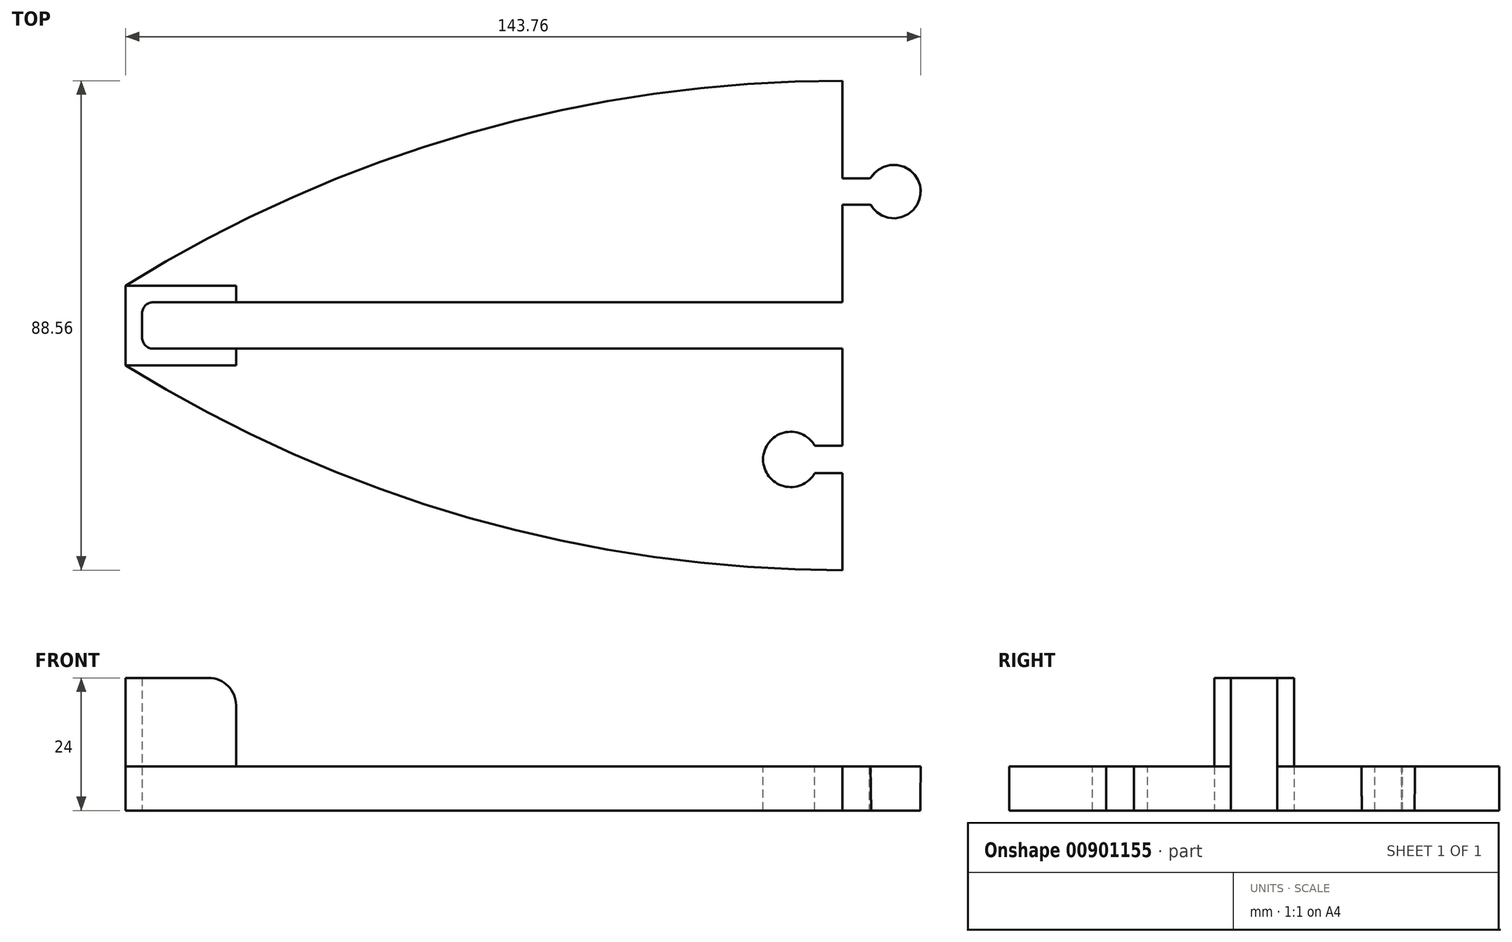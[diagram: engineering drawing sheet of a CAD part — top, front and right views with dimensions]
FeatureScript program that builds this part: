
annotation { "Feature Type Name" : "Feature", "Feature Type Description" : "" }
export const myFeature = defineFeature(function(context is Context, id is Id, definition is map)
    precondition{}
    {
        {
            assignVariable(context, id + "F0", {"name" : "gap", "anyValue" : .1});
        }
        {
            var Q0;
            Q0=qCreatedBy(makeId("Top.planeOp"),FACE);
            var sketch = newSketch(context, id + "F1", { "sketchPlane" : qUnion([Q0])});
            skLineSegment(sketch, "E0.bottom", {"start": v(126.6, -4.2) * mm, "end": v(-126.6, -4.2) * mm});
            skLineSegment(sketch, "E0.top", {"start": v(126.6, 4.2) * mm, "end": v(-126.6, 4.2) * mm});
            skLineSegment(sketch, "E0.left", {"start": v(126.6, -4.2) * mm, "end": v(126.6, 4.2) * mm});
            skLineSegment(sketch, "E0.right", {"start": v(-126.6, -4.2) * mm, "end": v(-126.6, 4.2) * mm});
            skPoint(sketch, "E0.middle", {"position": v(0, 0) * mm});
            skLineSegment(sketch, "E1.bottom", {"start": v(129.6, -7.2) * mm, "end": v(-129.6, -7.2) * mm});
            skLineSegment(sketch, "E1.top", {"start": v(129.6, 7.2) * mm, "end": v(-129.6, 7.2) * mm});
            skLineSegment(sketch, "E1.left", {"start": v(129.6, -7.2) * mm, "end": v(129.6, 7.2) * mm});
            skLineSegment(sketch, "E1.right", {"start": v(-129.6, -7.2) * mm, "end": v(-129.6, 7.2) * mm});
            skSolve(sketch);
        }
        {
            var Q0;
            Q0=qSketchRegion(id+"F1",true);
            extrude(context, id + "F2", {"entities" : qUnion([Q0]), "depth" : 24 * mm, "offsetDistance" : 25 * mm});
        }
        {
            var Q0;
            Q0=makeQuery(id+"F2.opExtrude","SWEPT_EDGE",EDGE,{"disambiguationData":[OSD([sQuery(id+"F1.wireOp",EDGE,"E0.bottom"),sQuery(id+"F1.wireOp",EDGE,"E0.left")])]});
            var Q1;
            Q1=makeQuery(id+"F2.opExtrude","SWEPT_EDGE",EDGE,{"disambiguationData":[OSD([sQuery(id+"F1.wireOp",EDGE,"E0.top"),sQuery(id+"F1.wireOp",EDGE,"E0.left")])]});
            var Q2;
            Q2=makeQuery(id+"F2.opExtrude","SWEPT_EDGE",EDGE,{"disambiguationData":[OSD([sQuery(id+"F1.wireOp",EDGE,"E0.bottom"),sQuery(id+"F1.wireOp",EDGE,"E0.right")])]});
            var Q3;
            Q3=makeQuery(id+"F2.opExtrude","SWEPT_EDGE",EDGE,{"disambiguationData":[OSD([sQuery(id+"F1.wireOp",EDGE,"E0.top"),sQuery(id+"F1.wireOp",EDGE,"E0.right")])]});
            fillet(context, id + "F3", {"entities" : qUnion([Q0, Q1, Q2, Q3]), "radius" : 2 * mm, "tangentPropagation" : true, "allowEdgeOverflow" : false});
        }
        {
            var Q0;
            Q0=qCreatedBy(makeId("Front.planeOp"),FACE);
            var sketch = newSketch(context, id + "F4", { "sketchPlane" : qUnion([Q0])});
            skArc(sketch, "E2", {"start": v(118.6, 0.75) * mm, "mid": v(124.26, 3.1) * mm, "end": v(126.6, 8.75) * mm});
            skLineSegment(sketch, "E3", {"start": v(126.6, 8.75) * mm, "end": v(129.6, 8.75) * mm});
            skLineSegment(sketch, "E4", {"start": v(129.6, 8.75) * mm, "end": v(129.6, 0) * mm});
            skLineSegment(sketch, "E5", {"start": v(118.6, 0.75) * mm, "end": v(118.6, 0) * mm});
            skLineSegment(sketch, "E6", {"start": v(118.6, 0) * mm, "end": v(129.6, 0) * mm});
            skSolve(sketch);
        }
        {
            var Q0;
            Q0=qSketchRegion(id+"F4",true);
            extrude(context, id + "F5", {"entities" : qUnion([Q0]), "operationType" : NewBodyOperationType.ADD, "endBound" : BoundingType.SYMMETRIC, "depth" : (8.5 + (2 * getVariable(context, 'gap'))) * mm, "offsetDistance" : 25 * mm});
        }
        {
            var Q0;
            Q0=makeQuery(id+"F2.opExtrude","CAP_FACE",FACE,{"disambiguationData":[OSD([sQuery(id+"F1.wireOp",EDGE,"E0.bottom"),sQuery(id+"F1.wireOp",EDGE,"E0.top"),sQuery(id+"F1.wireOp",EDGE,"E0.left"),sQuery(id+"F1.wireOp",EDGE,"E0.right"),sQuery(id+"F1.wireOp",EDGE,"E1.bottom"),sQuery(id+"F1.wireOp",EDGE,"E1.top"),sQuery(id+"F1.wireOp",EDGE,"E1.left"),sQuery(id+"F1.wireOp",EDGE,"E1.right")])],"isStart":false});
            var sketch = newSketch(context, id + "F6", { "sketchPlane" : qUnion([Q0])});
            skLineSegment(sketch, "E7.bottom", {"start": v(-109.6, -7.2) * mm, "end": v(109.6, -7.2) * mm});
            skLineSegment(sketch, "E7.top", {"start": v(-109.6, 7.2) * mm, "end": v(109.6, 7.2) * mm});
            skLineSegment(sketch, "E7.left", {"start": v(-109.6, -7.2) * mm, "end": v(-109.6, 7.2) * mm});
            skLineSegment(sketch, "E7.right", {"start": v(109.6, -7.2) * mm, "end": v(109.6, 7.2) * mm});
            skSolve(sketch);
        }
        {
            var Q0;
            Q0=qSketchRegion(id+"F6",true);
            extrude(context, id + "F7", {"entities" : qUnion([Q0]), "operationType" : NewBodyOperationType.REMOVE, "oppositeDirection" : true, "depth" : 16 * mm, "offsetDistance" : 25 * mm});
        }
        {
            var Q0;
            {var subQ1=sQuery(id+"F1.wireOp",EDGE,"E0.top");var subQ2=sQuery(id+"F6.wireOp",EDGE,"E7.left");Q0=makeQuery(id+"F7.boolean.opBoolean","COPY",EDGE,{"disambiguationData":[TD([makeQuery(id+"F2.opExtrude","SWEPT_FACE",FACE,{"disambiguationData":[OSD([subQ1])]})])],"derivedFrom":makeQuery(id+"F7.opExtrude","CAP_EDGE",EDGE,{"disambiguationData":[OSD([subQ2])],"isStart":true})});}
            var Q1;
            {var subQ0=sQuery(id+"F1.wireOp",EDGE,"E0.bottom");var subQ1=sQuery(id+"F6.wireOp",EDGE,"E7.left");Q1=makeQuery(id+"F7.boolean.opBoolean","COPY",EDGE,{"disambiguationData":[TD([makeQuery(id+"F2.opExtrude","SWEPT_FACE",FACE,{"disambiguationData":[OSD([subQ0])]})])],"derivedFrom":makeQuery(id+"F7.opExtrude","CAP_EDGE",EDGE,{"disambiguationData":[OSD([subQ1])],"isStart":true})});}
            var Q2;
            {var subQ1=sQuery(id+"F1.wireOp",EDGE,"E0.top");var subQ2=sQuery(id+"F6.wireOp",EDGE,"E7.right");Q2=makeQuery(id+"F7.boolean.opBoolean","COPY",EDGE,{"disambiguationData":[TD([makeQuery(id+"F2.opExtrude","SWEPT_FACE",FACE,{"disambiguationData":[OSD([subQ1])]})])],"derivedFrom":makeQuery(id+"F7.opExtrude","CAP_EDGE",EDGE,{"disambiguationData":[OSD([subQ2])],"isStart":true})});}
            var Q3;
            {var subQ0=sQuery(id+"F1.wireOp",EDGE,"E0.bottom");var subQ2=sQuery(id+"F6.wireOp",EDGE,"E7.right");Q3=makeQuery(id+"F7.boolean.opBoolean","COPY",EDGE,{"disambiguationData":[TD([makeQuery(id+"F2.opExtrude","SWEPT_FACE",FACE,{"disambiguationData":[OSD([subQ0])]})])],"derivedFrom":makeQuery(id+"F7.opExtrude","CAP_EDGE",EDGE,{"disambiguationData":[OSD([subQ2])],"isStart":true})});}
            fillet(context, id + "F8", {"entities" : qUnion([Q0, Q1, Q2, Q3]), "radius" : 5 * mm, "tangentPropagation" : true, "allowEdgeOverflow" : false});
        }
        {
            var Q0;
            Q0=qCreatedBy(makeId("Top.planeOp"),FACE);
            var sketch = newSketch(context, id + "F9", { "sketchPlane" : qUnion([Q0])});
            skArc(sketch, "E8", {"start": v(-129.6, -7.2) * mm, "mid": v(0, -44.28) * mm, "end": v(129.6, -7.2) * mm});
            skArc(sketch, "E9", {"start": v(129.6, 7.2) * mm, "mid": v(0, 44.28) * mm, "end": v(-129.6, 7.2) * mm});
            skLineSegment(sketch, "E10", {"start": v(-129.6, -7.2) * mm, "end": v(129.6, -7.2) * mm});
            skLineSegment(sketch, "E11", {"start": v(-129.6, 7.2) * mm, "end": v(129.6, 7.2) * mm});
            skSolve(sketch);
        }
        {
            var Q0;
            Q0=qSketchRegion(id+"F9",true);
            var Q1;
            {var subQ0=sQuery(id+"F6.wireOp",EDGE,"E7.left");var subQ1=sQuery(id+"F6.wireOp",EDGE,"E7.right");Q1=makeQuery(id+"F7.boolean.opBoolean","COPY",FACE,{"disambiguationData":[TD([makeQuery(id+"F2.opExtrude","SWEPT_FACE",FACE,{"disambiguationData":[OSD([sQuery(id+"F1.wireOp",EDGE,"E0.top")])]})])],"derivedFrom":makeQuery(id+"F7.opExtrude","CAP_FACE",FACE,{"disambiguationData":[OSD([sQuery(id+"F6.wireOp",EDGE,"E7.bottom"),sQuery(id+"F6.wireOp",EDGE,"E7.top"),subQ0,subQ1])],"isStart":false})});}
            extrude(context, id + "F10", {"entities" : qUnion([Q0]), "operationType" : NewBodyOperationType.ADD, "endBound" : BoundingType.UP_TO_SURFACE, "depth" : 3 * mm, "endBoundEntityFace" : qUnion([Q1]), "offsetDistance" : 25 * mm});
        }
        {
            var Q0;
            Q0=qCreatedBy(makeId("Right.planeOp"),FACE);
            var sketch = newSketch(context, id + "F11", { "sketchPlane" : qUnion([Q0])});
            skLineSegment(sketch, "E12.bottom", {"start": v(-49.8, 26) * mm, "end": v(56.3, 26) * mm});
            skLineSegment(sketch, "E12.top", {"start": v(-49.8, -11.33) * mm, "end": v(56.3, -11.33) * mm});
            skLineSegment(sketch, "E12.left", {"start": v(-49.8, 26) * mm, "end": v(-49.8, -11.33) * mm});
            skLineSegment(sketch, "E12.right", {"start": v(56.3, 26) * mm, "end": v(56.3, -11.33) * mm});
            skSolve(sketch);
        }
        {
            var Q0;
            Q0 = qSketchRegion(id + "F11", true);
            extrude(context, id + "F12", {"entities" : qUnion([Q0]), "operationType" : NewBodyOperationType.REMOVE, "endBound" : BoundingType.THROUGH_ALL, "depth" : 25 * mm, "offsetDistance" : 25 * mm});
        }
        {
            var Q0;
            Q0=makeQuery(id+"F10.opExtrude","CAP_FACE",FACE,{"disambiguationData":[OSD([sQuery(id+"F9.wireOp",EDGE,"E8"),sQuery(id+"F9.wireOp",EDGE,"E10")])],"isStart":false});
            var sketch = newSketch(context, id + "F13", { "sketchPlane" : qUnion([Q0])});
            skArc(sketch, "E13", {"start": v(-5, -21.74) * mm, "mid": v(-14.33, -24.24) * mm, "end": v(-5, -26.74) * mm});
            skLineSegment(sketch, "E14", {"start": v(-5, -21.74) * mm, "end": v(0, -21.74) * mm});
            skLineSegment(sketch, "E15", {"start": v(-5, -26.74) * mm, "end": v(0, -26.74) * mm});
            skLineSegment(sketch, "E16", {"start": v(0, -26.74) * mm, "end": v(0, -21.74) * mm});
            skLineSegment(sketch, "E17", {"start": v(0, -24.24) * mm, "end": v(-9.33, -24.24) * mm, "construction": true});
            skSolve(sketch);
        }
        {
            var Q0;
            Q0 = qSketchRegion(id + "F13", true);
            extrude(context, id + "F14", {"entities" : qUnion([Q0]), "operationType" : NewBodyOperationType.REMOVE, "endBound" : BoundingType.THROUGH_ALL, "oppositeDirection" : true, "depth" : 25 * mm, "offsetDistance" : 25 * mm});
        }
        {
            var Q0;
            Q0=makeQuery(id+"F10.opExtrude","CAP_FACE",FACE,{"disambiguationData":[OSD([sQuery(id+"F9.wireOp",EDGE,"E9"),sQuery(id+"F9.wireOp",EDGE,"E11")])],"isStart":false});
            var sketch = newSketch(context, id + "F15", { "sketchPlane" : qUnion([Q0])});
            skLineSegment(sketch, "E18", {"start": v(9.31, 24.24) * mm, "end": v(0, 24.24) * mm});
            skLineSegment(sketch, "E19", {"start": v(0, 26.64) * mm, "end": v(5.1, 26.64) * mm});
            skLineSegment(sketch, "E20", {"start": v(0, 21.84) * mm, "end": v(5.1, 21.84) * mm});
            skLineSegment(sketch, "E21", {"start": v(0, 21.84) * mm, "end": v(0, 26.64) * mm});
            skArc(sketch, "E22", {"start": v(5.1, 21.84) * mm, "mid": v(14.16, 24.24) * mm, "end": v(5.1, 26.64) * mm});
            skSolve(sketch);
        }
        {
            var Q0;
            Q0 = qSketchRegion(id + "F15", true);
            var Q1;
            {var subQ0=sQuery(id+"F4.wireOp",EDGE,"E6");Q1=makeQuery(id+"F10.boolean.opBoolean","MERGE",FACE,{"derivedFrom":[makeQuery(id+"Frt0GUivWiWnZhL_1.1.F5.boolean.opBoolean","MERGE",FACE,{"derivedFrom":[makeQuery(id+"F5.boolean.opBoolean","MERGE",FACE,{"derivedFrom":[makeQuery(id+"F2.opExtrude","CAP_FACE",FACE,{"disambiguationData":[OSD([sQuery(id+"F1.wireOp",EDGE,"E0.bottom"),sQuery(id+"F1.wireOp",EDGE,"E0.top"),sQuery(id+"F1.wireOp",EDGE,"E0.left"),sQuery(id+"F1.wireOp",EDGE,"E0.right"),sQuery(id+"F1.wireOp",EDGE,"E1.bottom"),sQuery(id+"F1.wireOp",EDGE,"E1.top"),sQuery(id+"F1.wireOp",EDGE,"E1.left"),sQuery(id+"F1.wireOp",EDGE,"E1.right")])],"isStart":true}),makeQuery(id+"F5.opExtrude","SWEPT_FACE",FACE,{"disambiguationData":[OSD([subQ0])]})]}),makeQuery(id+"Frt0GUivWiWnZhL_1.1.F5.opExtrude","SWEPT_FACE",FACE,{"disambiguationData":[OSD([subQ0])]})]}),makeQuery(id+"F10.opExtrude","CAP_FACE",FACE,{"disambiguationData":[OSD([sQuery(id+"F9.wireOp",EDGE,"E8"),sQuery(id+"F9.wireOp",EDGE,"E10")])],"isStart":true}),makeQuery(id+"F10.opExtrude","CAP_FACE",FACE,{"disambiguationData":[OSD([sQuery(id+"F9.wireOp",EDGE,"E9"),sQuery(id+"F9.wireOp",EDGE,"E11")])],"isStart":true})]});}
            extrude(context, id + "F16", {"entities" : qUnion([Q0]), "operationType" : NewBodyOperationType.ADD, "endBound" : BoundingType.UP_TO_SURFACE, "oppositeDirection" : true, "depth" : 25 * mm, "endBoundEntityFace" : qUnion([Q1]), "offsetDistance" : 25 * mm});
        }
        {
            var Q0;
            Q0=makeQuery(id+"F16.opExtrude","SWEPT_FACE",FACE,{"disambiguationData":[OSD([sQuery(id+"F15.wireOp",EDGE,"E20")])]});
            var sketch = newSketch(context, id + "F17", { "sketchPlane" : qUnion([Q0])});
            skLineSegment(sketch, "E23", {"start": v(5.1, 0) * mm, "end": v(5.2, 0) * mm});
            skLineSegment(sketch, "E24", {"start": v(5.1, 0) * mm, "end": v(5.1, 8) * mm});
            skLineSegment(sketch, "E25", {"start": v(5.1, 8) * mm, "end": v(5.2, 0) * mm});
            skSolve(sketch);
        }
        {
            var Q0;
            {var subQ0=sQuery(id+"F4.wireOp",EDGE,"E6");Q0=makeQuery(id+"F16.boolean.opBoolean","MERGE",FACE,{"derivedFrom":[makeQuery(id+"F10.boolean.opBoolean","MERGE",FACE,{"derivedFrom":[makeQuery(id+"Frt0GUivWiWnZhL_1.1.F5.boolean.opBoolean","MERGE",FACE,{"derivedFrom":[makeQuery(id+"F5.boolean.opBoolean","MERGE",FACE,{"derivedFrom":[makeQuery(id+"F2.opExtrude","CAP_FACE",FACE,{"disambiguationData":[OSD([sQuery(id+"F1.wireOp",EDGE,"E0.bottom"),sQuery(id+"F1.wireOp",EDGE,"E0.top"),sQuery(id+"F1.wireOp",EDGE,"E0.left"),sQuery(id+"F1.wireOp",EDGE,"E0.right"),sQuery(id+"F1.wireOp",EDGE,"E1.bottom"),sQuery(id+"F1.wireOp",EDGE,"E1.top"),sQuery(id+"F1.wireOp",EDGE,"E1.left"),sQuery(id+"F1.wireOp",EDGE,"E1.right")])],"isStart":true}),makeQuery(id+"F5.opExtrude","SWEPT_FACE",FACE,{"disambiguationData":[OSD([subQ0])]})]}),makeQuery(id+"Frt0GUivWiWnZhL_1.1.F5.opExtrude","SWEPT_FACE",FACE,{"disambiguationData":[OSD([subQ0])]})]}),makeQuery(id+"F10.opExtrude","CAP_FACE",FACE,{"disambiguationData":[OSD([sQuery(id+"F9.wireOp",EDGE,"E8"),sQuery(id+"F9.wireOp",EDGE,"E10")])],"isStart":true}),makeQuery(id+"F10.opExtrude","CAP_FACE",FACE,{"disambiguationData":[OSD([sQuery(id+"F9.wireOp",EDGE,"E9"),sQuery(id+"F9.wireOp",EDGE,"E11")])],"isStart":true})]}),makeQuery(id+"F16.opExtrude","CAP_FACE",FACE,{"disambiguationData":[OSD([sQuery(id+"F15.wireOp",EDGE,"E19"),sQuery(id+"F15.wireOp",EDGE,"E20"),sQuery(id+"F15.wireOp",EDGE,"E21"),sQuery(id+"F15.wireOp",EDGE,"E22")])],"isStart":false})]});}
            var sketch = newSketch(context, id + "F18", { "sketchPlane" : qUnion([Q0])});
            skArc(sketch, "E26", {"start": v(5.1, -26.64) * mm, "mid": v(14.16, -24.24) * mm, "end": v(5.1, -21.84) * mm});
            skSolve(sketch);
        }
        {
            var Q0;
            Q0 = qSketchRegion(id + "F17", true);
            var Q1;
            Q1 = qBodyType(qCreatedBy(id + "F18" ,EDGE), BodyType.WIRE);
            sweep(context, id + "F19", {"operationType" : NewBodyOperationType.REMOVE, "profiles" : qUnion([Q0]), "path" : qUnion([Q1])});
        }
        {
            var Q0;
            Q0=makeQuery(id+"F19.boolean.opBoolean","MERGE",EDGE,{"derivedFrom":[makeQuery(id+"F16.opExtrude","SWEPT_EDGE",EDGE,{"disambiguationData":[OSD([sQuery(id+"F15.wireOp",EDGE,"E19"),sQuery(id+"F15.wireOp",EDGE,"E22")])]})],"fromTools":[makeQuery(id+"F19.opSweep","CAP_EDGE",EDGE,{"disambiguationData":[OSD([sQuery(id+"F17.wireOp",EDGE,"E24"),sQuery(id+"F18.wireOp",VERTEX,"E26.start")])],"isStart":false})]});
            chamfer(context, id + "F20", {"entities" : qUnion([Q0]), "width" : .5 * mm, "tangentPropagation" : true});
        }
        {
            var Q0;
            Q0=makeQuery(id+"F20.opChamfer","BLEND_EDGE",EDGE,{"blendedFrom":[makeQuery(id+"F19.boolean.opBoolean","MERGE",EDGE,{"derivedFrom":[makeQuery(id+"F16.opExtrude","SWEPT_EDGE",EDGE,{"disambiguationData":[OSD([sQuery(id+"F15.wireOp",EDGE,"E19"),sQuery(id+"F15.wireOp",EDGE,"E22")])]})],"fromTools":[makeQuery(id+"F19.opSweep","CAP_EDGE",EDGE,{"disambiguationData":[OSD([sQuery(id+"F17.wireOp",EDGE,"E24"),sQuery(id+"F18.wireOp",VERTEX,"E26.start")])],"isStart":false})]}),makeQuery(id+"F19.boolean.opBoolean","COPY",FACE,{"derivedFrom":makeQuery(id+"F19.opSweep","SWEPT_FACE",FACE,{"disambiguationData":[OSD([sQuery(id+"F17.wireOp",EDGE,"E25"),sQuery(id+"F18.wireOp",EDGE,"E26")])]})})],"blendedInto":[makeQuery(id+"F19.boolean.opBoolean","COPY",FACE,{"derivedFrom":makeQuery(id+"F19.opSweep","SWEPT_FACE",FACE,{"disambiguationData":[OSD([sQuery(id+"F17.wireOp",EDGE,"E25"),sQuery(id+"F18.wireOp",EDGE,"E26")])]})})]});
            fillet(context, id + "F21", {"entities" : qUnion([Q0]), "radius" : .5 * mm, "tangentPropagation" : true, "allowEdgeOverflow" : false});
        }
    });
